# Revit family: Courier_Boxes-Salsbury_Industries-Mailbox
name_source: partatom
category: Specialty Equipment
revit_build: Autodesk Revit 2016 (Build: 20150714_1515(x64)
units: mm (PartAtom-declared; Revit-internal decimal feet)

## family parameters
Always vertical = Yes
Cut with Voids When Loaded = No
OmniClass Number = 23.40.90.14.11
OmniClass Title = Mail Boxes
Part Type = Normal
Room Calculation Point = No
Round Connector Dimension = Use Diameter
Shared = No
Work Plane-Based = No

## types (1)
- 4975
    Assembly Code = C1030910
    Assembly Description = Mailboxes
    Depth = 26 "
    Description = Package drop opening; user access locking compartment
    Height = 49 "
    Lock Material = Stainless Steel - Salsbury Finish -  Polished
    Manufacturer = Salsbury Industries
    MasterFormat Number = 10 55 00
    MasterFormat Title = Postal Specialties
    Model = 4975
    OmniClass 23 Number = 23.40.90.14.11
    OmniClass 23 Title = Mail Boxes
    Type Comments = Courier Box
    URL = www.mailboxes.com
    Version = 1.0 (04/30/19)
    Width = 20 "

## geometry (parser evidence)
native form markers: Sweep x2
no freeform markers — native parametric forms only
